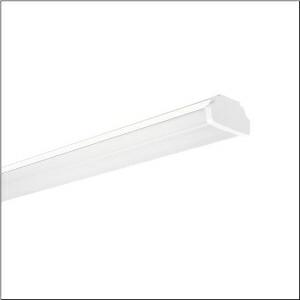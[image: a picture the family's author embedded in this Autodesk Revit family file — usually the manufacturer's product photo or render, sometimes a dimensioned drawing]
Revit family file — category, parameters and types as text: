
# Revit family: modario_r__31_gen_2_53bm812mv4a5c2_e17c
name_source: partatom
category: Lighting Fixtures
units: mm (PartAtom-declared; Revit-internal decimal feet)

## family parameters
Cut with Voids When Loaded = No
Host = Face
Light Source = No
Part Type = Normal
Room Calculation Point = No
Round Connector Dimension = Use Diameter
Shared = No

## types (1)
- --- (1 x LED, 10960 lm, 60.5 W, 4000K)
    Apparent Load = 61 VA
    CIE Flux Codes = 47 80 95 93 100
    Color Rendering = 80
    Color Temperature = 4000K
    Default Elevation = 1800 mm
    Description = Modario® 31 Gen.2, luminaire insert, of sheet steel, coil coated, white, length: 1.495mm, width: 81mm, height: 82mm, 5x system unit, system units: 299mm, LED rated luminous flux: 10.960lm, light colour: 840, control gear: ON/OFF Multilumen, control gear: ECG, with plug, 3-pole, with phase selection, mains connection: 220..240V, AC, 50/60Hz, rated input power: 61W, through-wiring accessed according to module size, primary optical cover: cover, of PMMA, light emission: direct distribution, primary light characteristic: symmetric, protection rating (complete): IP20, protection rating (LED compartment): IP50, insulation class (complete): insulation class I (protective earthing), certification: CE, ENEC, VDE, UKCA, impact resistance: IK03, permissible ambient temperature for indoor applications: -35..+40°C, corresponds to IFS (International Featured Standards) requirements for safety and quality in the food industry, reducing of maximum allowable ambient temperature of 5°C with ceiling mounting, IP40 when using the optional accessory 5TP9018, packaging unit: 1 piece
    Height = 92 mm
    Lamp = 1 x LED
    Lamp Light Flux = 10960 lm
    Lamp Power = 60.5 W
    Lamp count = 1
    Length = 1495 mm
    Luminous efficacy = 181 lm/W
    Manufacturer = Siteco
    ModVariant = No
    Model = 53BM812MV4A5C2
    Mounting Place = Ceiling
    Mounting Type = Pendant
    Number of Poles = 1
    OnlyDefault = Yes
    Power Factor = 1
    Product Name = Modario® 31 Gen.2
    Product group = luminaire insert
    ProductGroupID = 902
    Protection Class = Protection class I
    Protection Degree = IP 20
    RLX_Detail_Level = 1
    RLX_Emergency_Light_Flux = 0 lm
    RLX_Emergency_Type = 0
    RLX_Emergency_Type_DB = No
    RlxData = <blob elided: 39977 chars, md5=3004ba17>
    Socket = socket
    Standby Power = 0 W
    System Light Flux = 10960 lm
    System Power = 61 W
    Type Comments = factory setting: luminous flux: 100 % | (A | C | E) | 140 mA
    Type Image = l_1341886.jpg
    URL = http://relux.com
    VarID = @adj_043406
    Voltage = 0 V
    Weight = 0.00 kg
    Width = 81 mm

## geometry (parser evidence)
native form markers: Blend x4, Sweep x13
no freeform markers — native parametric forms only
